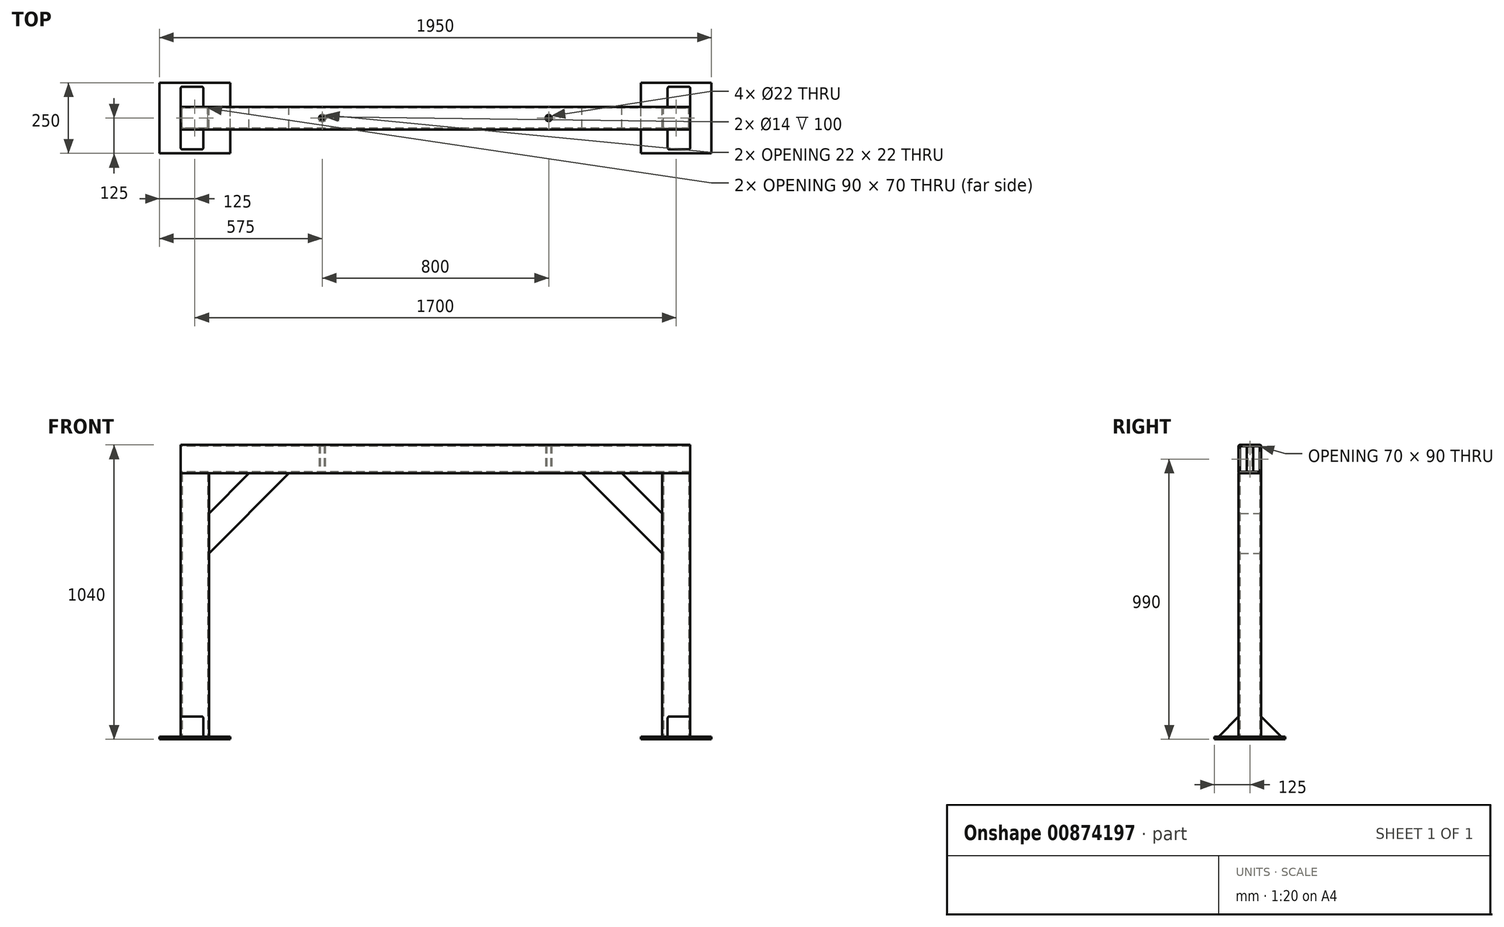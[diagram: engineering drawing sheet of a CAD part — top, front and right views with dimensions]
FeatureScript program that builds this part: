
annotation { "Feature Type Name" : "Feature", "Feature Type Description" : "" }
export const myFeature = defineFeature(function(context is Context, id is Id, definition is map)
    precondition{}
    {
        {
            var Q0;
            Q0=qCreatedBy(makeId("Top.planeOp"),FACE);
            var sketch = newSketch(context, id + "F0", { "sketchPlane" : qUnion([Q0])});
            skLineSegment(sketch, "E0.bottom", {"start": v(-804, -40) * mm, "end": v(-896, -40) * mm});
            skLineSegment(sketch, "E0.top", {"start": v(-804, 40) * mm, "end": v(-896, 40) * mm});
            skLineSegment(sketch, "E0.left", {"start": v(-800, -36) * mm, "end": v(-800, 36) * mm});
            skLineSegment(sketch, "E0.right", {"start": v(-900, -36) * mm, "end": v(-900, 36) * mm});
            skPoint(sketch, "E0.middle", {"position": v(-850, 0) * mm});
            skLineSegment(sketch, "E1.bottom", {"start": v(-808, -35) * mm, "end": v(-892, -35) * mm});
            skLineSegment(sketch, "E1.top", {"start": v(-808, 35) * mm, "end": v(-892, 35) * mm});
            skLineSegment(sketch, "E1.left", {"start": v(-805, -32) * mm, "end": v(-805, 32) * mm});
            skLineSegment(sketch, "E1.right", {"start": v(-895, -32) * mm, "end": v(-895, 32) * mm});
            skPoint(sketch, "E2.visualSharp", {"position": v(-895, 35) * mm});
            skArc(sketch, "E2.filletArc", {"start": v(-892, 35) * mm, "mid": v(-894.12, 34.12) * mm, "end": v(-895, 32) * mm});
            skPoint(sketch, "E3.visualSharp", {"position": v(-805, 35) * mm});
            skArc(sketch, "E3.filletArc", {"start": v(-805, 32) * mm, "mid": v(-805.88, 34.12) * mm, "end": v(-808, 35) * mm});
            skPoint(sketch, "E4.visualSharp", {"position": v(-805, -35) * mm});
            skArc(sketch, "E4.filletArc", {"start": v(-808, -35) * mm, "mid": v(-805.88, -34.12) * mm, "end": v(-805, -32) * mm});
            skPoint(sketch, "E5.visualSharp", {"position": v(-895, -35) * mm});
            skArc(sketch, "E5.filletArc", {"start": v(-895, -32) * mm, "mid": v(-894.12, -34.12) * mm, "end": v(-892, -35) * mm});
            skPoint(sketch, "E6.visualSharp", {"position": v(-900, 40) * mm});
            skArc(sketch, "E6.filletArc", {"start": v(-896, 40) * mm, "mid": v(-898.83, 38.83) * mm, "end": v(-900, 36) * mm});
            skPoint(sketch, "E7.visualSharp", {"position": v(-800, 40) * mm});
            skArc(sketch, "E7.filletArc", {"start": v(-800, 36) * mm, "mid": v(-801.17, 38.83) * mm, "end": v(-804, 40) * mm});
            skPoint(sketch, "E8.visualSharp", {"position": v(-800, -40) * mm});
            skArc(sketch, "E8.filletArc", {"start": v(-804, -40) * mm, "mid": v(-801.17, -38.83) * mm, "end": v(-800, -36) * mm});
            skPoint(sketch, "E9.visualSharp", {"position": v(-900, -40) * mm});
            skArc(sketch, "E9.filletArc", {"start": v(-900, -36) * mm, "mid": v(-898.83, -38.83) * mm, "end": v(-896, -40) * mm});
            skArc(sketch, "E10.MirrorCS", {"start": v(808, -35) * mm, "mid": v(805.88, -34.12) * mm, "end": v(805, -32) * mm});
            skArc(sketch, "E11.MirrorCS", {"start": v(800, 36) * mm, "mid": v(801.17, 38.83) * mm, "end": v(804, 40) * mm});
            skArc(sketch, "E12.MirrorCS", {"start": v(804, -40) * mm, "mid": v(801.17, -38.83) * mm, "end": v(800, -36) * mm});
            skArc(sketch, "E13.MirrorCS", {"start": v(892, 35) * mm, "mid": v(894.12, 34.12) * mm, "end": v(895, 32) * mm});
            skArc(sketch, "E14.MirrorCS", {"start": v(896, 40) * mm, "mid": v(898.83, 38.83) * mm, "end": v(900, 36) * mm});
            skArc(sketch, "E15.MirrorCS", {"start": v(805, 32) * mm, "mid": v(805.88, 34.12) * mm, "end": v(808, 35) * mm});
            skArc(sketch, "E16.MirrorCS", {"start": v(895, -32) * mm, "mid": v(894.12, -34.12) * mm, "end": v(892, -35) * mm});
            skArc(sketch, "E17.MirrorCS", {"start": v(900, -36) * mm, "mid": v(898.83, -38.83) * mm, "end": v(896, -40) * mm});
            skLineSegment(sketch, "E18.MirrorCS", {"start": v(900, -36) * mm, "end": v(900, 36) * mm});
            skPoint(sketch, "E19.MirrorP", {"position": v(850, 0) * mm});
            skLineSegment(sketch, "E20.MirrorCS", {"start": v(804, -40) * mm, "end": v(896, -40) * mm});
            skPoint(sketch, "E21.MirrorP", {"position": v(805, 35) * mm});
            skLineSegment(sketch, "E22.MirrorCS", {"start": v(805, -32) * mm, "end": v(805, 32) * mm});
            skLineSegment(sketch, "E23.MirrorCS", {"start": v(895, -32) * mm, "end": v(895, 32) * mm});
            skLineSegment(sketch, "E24.MirrorCS", {"start": v(800, -36) * mm, "end": v(800, 36) * mm});
            skLineSegment(sketch, "E25.MirrorCS", {"start": v(808, -35) * mm, "end": v(892, -35) * mm});
            skPoint(sketch, "E26.MirrorP", {"position": v(895, 35) * mm});
            skPoint(sketch, "E27.MirrorP", {"position": v(900, 40) * mm});
            skPoint(sketch, "E28.MirrorP", {"position": v(800, 40) * mm});
            skPoint(sketch, "E29.MirrorP", {"position": v(900, -40) * mm});
            skPoint(sketch, "E30.MirrorP", {"position": v(805, -35) * mm});
            skLineSegment(sketch, "E31.MirrorCS", {"start": v(808, 35) * mm, "end": v(892, 35) * mm});
            skLineSegment(sketch, "E32.MirrorCS", {"start": v(804, 40) * mm, "end": v(896, 40) * mm});
            skPoint(sketch, "E33.MirrorP", {"position": v(895, -35) * mm});
            skPoint(sketch, "E34.MirrorP", {"position": v(800, -40) * mm});
            skSolve(sketch);
        }
        {
            var Q0;
            Q0=qSketchRegion(id+"F0",true);
            extrude(context, id + "F1", {"entities" : qUnion([Q0]), "depth" : 930 * mm, "offsetDistance" : 25 * mm});
        }
        {
            var Q0;
            Q0=makeQuery(id+"F1.opExtrude","SWEPT_FACE",FACE,{"disambiguationData":[OSD([sQuery(id+"F0.wireOp",EDGE,"E0.right")])]});
            var sketch = newSketch(context, id + "F2", { "sketchPlane" : qUnion([Q0])});
            skLineSegment(sketch, "E35.bottom", {"start": v(36, 930) * mm, "end": v(-36, 930) * mm});
            skLineSegment(sketch, "E35.top", {"start": v(36, 1030) * mm, "end": v(-36, 1030) * mm});
            skLineSegment(sketch, "E35.left", {"start": v(40, 934) * mm, "end": v(40, 1026) * mm});
            skLineSegment(sketch, "E35.right", {"start": v(-40, 934) * mm, "end": v(-40, 1026) * mm});
            skPoint(sketch, "E35.middle", {"position": v(0, 980) * mm});
            skPoint(sketch, "E35.middle.positionSnap0", {"position": v(0, 930) * mm});
            skPoint(sketch, "E35.centerSnap0", {"position": v(0, 930) * mm});
            skLineSegment(sketch, "E36.bottom", {"start": v(32, 935) * mm, "end": v(-32, 935) * mm});
            skLineSegment(sketch, "E36.top", {"start": v(32, 1025) * mm, "end": v(-32, 1025) * mm});
            skLineSegment(sketch, "E36.left", {"start": v(35, 938) * mm, "end": v(35, 1022) * mm});
            skLineSegment(sketch, "E36.right", {"start": v(-35, 938) * mm, "end": v(-35, 1022) * mm});
            skPoint(sketch, "E37.visualSharp", {"position": v(-35, 1025) * mm});
            skArc(sketch, "E37.filletArc", {"start": v(-32, 1025) * mm, "mid": v(-34.12, 1024.12) * mm, "end": v(-35, 1022) * mm});
            skPoint(sketch, "E38.visualSharp", {"position": v(35, 1025) * mm});
            skArc(sketch, "E38.filletArc", {"start": v(35, 1022) * mm, "mid": v(34.12, 1024.12) * mm, "end": v(32, 1025) * mm});
            skPoint(sketch, "E39.visualSharp", {"position": v(35, 935) * mm});
            skArc(sketch, "E39.filletArc", {"start": v(32, 935) * mm, "mid": v(34.12, 935.88) * mm, "end": v(35, 938) * mm});
            skPoint(sketch, "E40.visualSharp", {"position": v(-35, 935) * mm});
            skArc(sketch, "E40.filletArc", {"start": v(-35, 938) * mm, "mid": v(-34.12, 935.88) * mm, "end": v(-32, 935) * mm});
            skPoint(sketch, "E41.visualSharp", {"position": v(-40, 1030) * mm});
            skArc(sketch, "E41.filletArc", {"start": v(-36, 1030) * mm, "mid": v(-38.83, 1028.83) * mm, "end": v(-40, 1026) * mm});
            skPoint(sketch, "E42.visualSharp", {"position": v(40, 1030) * mm});
            skArc(sketch, "E42.filletArc", {"start": v(40, 1026) * mm, "mid": v(38.83, 1028.83) * mm, "end": v(36, 1030) * mm});
            skPoint(sketch, "E43.visualSharp", {"position": v(40, 930) * mm});
            skArc(sketch, "E43.filletArc", {"start": v(36, 930) * mm, "mid": v(38.83, 931.17) * mm, "end": v(40, 934) * mm});
            skPoint(sketch, "E44.visualSharp", {"position": v(-40, 930) * mm});
            skArc(sketch, "E44.filletArc", {"start": v(-40, 934) * mm, "mid": v(-38.83, 931.17) * mm, "end": v(-36, 930) * mm});
            skSolve(sketch);
        }
        {
            var Q0;
            Q0=makeQuery(id+"F2.imprint","IMPRINT",FACE,{"disambiguationData":[TD([[makeQuery(id+"F2.imprint","IMPRINT",EDGE,{"derivedFrom":sQuery(id+"F2.wireOp",EDGE,"E35.bottom")}),-1.0]])]});
            extrude(context, id + "F3", {"entities" : qUnion([Q0]), "oppositeDirection" : true, "depth" : 1800 * mm, "offsetDistance" : 25 * mm});
        }
        {
            var Q0;
            Q0=qCreatedBy(makeId("Front.planeOp"),FACE);
            var sketch = newSketch(context, id + "F4", { "sketchPlane" : qUnion([Q0])});
            skLineSegment(sketch, "E45.0", {"start": v(800, 788.58) * mm, "end": v(800, 647.16) * mm});
            skLineSegment(sketch, "E46.0", {"start": v(658.58, 930) * mm, "end": v(517.16, 930) * mm});
            skLineSegment(sketch, "E47", {"start": v(800, 647.16) * mm, "end": v(517.16, 930) * mm});
            skLineSegment(sketch, "E48.0", {"start": v(800, 788.58) * mm, "end": v(658.58, 930) * mm});
            skPoint(sketch, "E49.orphan", {"position": v(900, 930) * mm});
            skPoint(sketch, "E50.orphan", {"position": v(-900, 930) * mm});
            skPoint(sketch, "E51.orphan", {"position": v(800, 0) * mm});
            skLineSegment(sketch, "E52.MirrorCS", {"start": v(-800, 788.58) * mm, "end": v(-658.58, 930) * mm});
            skLineSegment(sketch, "E53.MirrorCS", {"start": v(-800, 647.16) * mm, "end": v(-517.16, 930) * mm});
            skLineSegment(sketch, "E54.MirrorCS", {"start": v(-800, 788.58) * mm, "end": v(-800, 647.16) * mm});
            skLineSegment(sketch, "E55.MirrorCS", {"start": v(-658.58, 930) * mm, "end": v(-517.16, 930) * mm});
            skPoint(sketch, "E56.orphan", {"position": v(800, 930) * mm});
            skPoint(sketch, "E57.orphan", {"position": v(-800, 930) * mm});
            skSolve(sketch);
        }
        {
            var Q0;
            Q0=qSketchRegion(id+"F4",true);
            extrude(context, id + "F5", {"entities" : qUnion([Q0]), "endBound" : BoundingType.SYMMETRIC, "depth" : 80 * mm, "offsetDistance" : 25 * mm});
        }
        {
            var Q0;
            Q0=makeQuery(id+"F5.opExtrude","CAP_EDGE",EDGE,{"disambiguationData":[OSD([sQuery(id+"F4.wireOp",EDGE,"E47")])],"isStart":true});
            var Q1;
            Q1=makeQuery(id+"F5.opExtrude","CAP_EDGE",EDGE,{"disambiguationData":[OSD([sQuery(id+"F4.wireOp",EDGE,"E47")])],"isStart":false});
            var Q2;
            Q2=makeQuery(id+"F5.opExtrude","CAP_EDGE",EDGE,{"disambiguationData":[OSD([sQuery(id+"F4.wireOp",EDGE,"E53.MirrorCS")])],"isStart":true});
            var Q3;
            Q3=makeQuery(id+"F5.opExtrude","CAP_EDGE",EDGE,{"disambiguationData":[OSD([sQuery(id+"F4.wireOp",EDGE,"E53.MirrorCS")])],"isStart":false});
            fillet(context, id + "F6", {"entities" : qUnion([Q0, Q1, Q2, Q3]), "radius" : 5 * mm, "tangentPropagation" : true, "allowEdgeOverflow" : false});
        }
        {
            var Q0;
            Q0=makeQuery(id+"F1.opExtrude","CAP_FACE",FACE,{"disambiguationData":[OSD([sQuery(id+"F0.wireOp",EDGE,"E10.MirrorCS"),sQuery(id+"F0.wireOp",EDGE,"E11.MirrorCS"),sQuery(id+"F0.wireOp",EDGE,"E12.MirrorCS"),sQuery(id+"F0.wireOp",EDGE,"E13.MirrorCS"),sQuery(id+"F0.wireOp",EDGE,"E14.MirrorCS"),sQuery(id+"F0.wireOp",EDGE,"E15.MirrorCS"),sQuery(id+"F0.wireOp",EDGE,"E16.MirrorCS"),sQuery(id+"F0.wireOp",EDGE,"E17.MirrorCS"),sQuery(id+"F0.wireOp",EDGE,"E18.MirrorCS"),sQuery(id+"F0.wireOp",EDGE,"E20.MirrorCS"),sQuery(id+"F0.wireOp",EDGE,"E22.MirrorCS"),sQuery(id+"F0.wireOp",EDGE,"E23.MirrorCS"),sQuery(id+"F0.wireOp",EDGE,"E24.MirrorCS"),sQuery(id+"F0.wireOp",EDGE,"E25.MirrorCS"),sQuery(id+"F0.wireOp",EDGE,"E31.MirrorCS"),sQuery(id+"F0.wireOp",EDGE,"E32.MirrorCS")])],"isStart":true});
            var sketch = newSketch(context, id + "F7", { "sketchPlane" : qUnion([Q0])});
            skLineSegment(sketch, "E58.bottom", {"start": v(725, 125) * mm, "end": v(975, 125) * mm});
            skLineSegment(sketch, "E58.top", {"start": v(725, -125) * mm, "end": v(975, -125) * mm});
            skLineSegment(sketch, "E58.left", {"start": v(725, 125) * mm, "end": v(725, -125) * mm});
            skLineSegment(sketch, "E58.right", {"start": v(975, 125) * mm, "end": v(975, -125) * mm});
            skPoint(sketch, "E58.middle", {"position": v(850, 0) * mm});
            skLineSegment(sketch, "E59.MirrorCS", {"start": v(-725, 125) * mm, "end": v(-975, 125) * mm});
            skLineSegment(sketch, "E60.MirrorCS", {"start": v(-725, -125) * mm, "end": v(-975, -125) * mm});
            skLineSegment(sketch, "E61.MirrorCS", {"start": v(-975, 125) * mm, "end": v(-975, -125) * mm});
            skPoint(sketch, "E62.MirrorP", {"position": v(-850, 0) * mm});
            skLineSegment(sketch, "E63.MirrorCS", {"start": v(-725, 125) * mm, "end": v(-725, -125) * mm});
            skSolve(sketch);
        }
        {
            var Q0;
            Q0=qSketchRegion(id+"F7",true);
            extrude(context, id + "F8", {"entities" : qUnion([Q0]), "depth" : 10 * mm, "offsetDistance" : 25 * mm});
        }
        {
            var Q0;
            Q0=makeQuery(id+"F1.opExtrude","SWEPT_FACE",FACE,{"disambiguationData":[OSD([sQuery(id+"F0.wireOp",EDGE,"E18.MirrorCS")])]});
            var sketch = newSketch(context, id + "F9", { "sketchPlane" : qUnion([Q0])});
            skLineSegment(sketch, "E64.0", {"start": v(40, 70.71) * mm, "end": v(40, 0) * mm});
            skLineSegment(sketch, "E65.0", {"start": v(40, 0) * mm, "end": v(110.71, 0) * mm});
            skLineSegment(sketch, "E66", {"start": v(40, 70.71) * mm, "end": v(110.71, 0) * mm});
            skPoint(sketch, "E67.orphan", {"position": v(40, 930) * mm});
            skPoint(sketch, "E68.orphan", {"position": v(125, 0) * mm});
            skPoint(sketch, "E69.orphan", {"position": v(-125, 0) * mm});
            skLineSegment(sketch, "E70.MirrorCS", {"start": v(-40, 70.71) * mm, "end": v(-110.71, 0) * mm});
            skLineSegment(sketch, "E71.MirrorCS", {"start": v(-40, 0) * mm, "end": v(-110.71, 0) * mm});
            skLineSegment(sketch, "E72.MirrorCS", {"start": v(-40, 70.71) * mm, "end": v(-40, 0) * mm});
            skSolve(sketch);
        }
        {
            var Q0;
            Q0=makeQuery(id+"F9.imprint","IMPRINT",FACE,{"disambiguationData":[TD([[makeQuery(id+"F9.imprint","IMPRINT",EDGE,{"derivedFrom":sQuery(id+"F9.wireOp",EDGE,"E70.MirrorCS")}),1.0]])]});
            var Q1;
            Q1=makeQuery(id+"F9.imprint","IMPRINT",FACE,{"disambiguationData":[TD([[makeQuery(id+"F9.imprint","IMPRINT",EDGE,{"derivedFrom":sQuery(id+"F9.wireOp",EDGE,"E64.0")}),1.0]])]});
            extrude(context, id + "F10", {"entities" : qUnion([Q0, Q1]), "oppositeDirection" : true, "depth" : 80 * mm, "offsetDistance" : 25 * mm});
        }
        {
            var Q0;
            Q0=makeQuery(id+"F10.opExtrude","CAP_EDGE",EDGE,{"disambiguationData":[OSD([sQuery(id+"F9.wireOp",EDGE,"E66")])],"isStart":true});
            var Q1;
            Q1=makeQuery(id+"F10.opExtrude","CAP_EDGE",EDGE,{"disambiguationData":[OSD([sQuery(id+"F9.wireOp",EDGE,"E66")])],"isStart":false});
            var Q2;
            Q2=makeQuery(id+"F10.opExtrude","CAP_EDGE",EDGE,{"disambiguationData":[OSD([sQuery(id+"F9.wireOp",EDGE,"E70.MirrorCS")])],"isStart":true});
            var Q3;
            Q3=makeQuery(id+"F10.opExtrude","CAP_EDGE",EDGE,{"disambiguationData":[OSD([sQuery(id+"F9.wireOp",EDGE,"E70.MirrorCS")])],"isStart":false});
            fillet(context, id + "F11", {"entities" : qUnion([Q0, Q1, Q2, Q3]), "radius" : 5 * mm, "tangentPropagation" : true, "allowEdgeOverflow" : false});
        }
        {
            var Q0;
            Q0=makeQuery(id+"F10.opExtrude","SWEPT_BODY",BODY,{"disambiguationData":[OSD([sQuery(id+"F9.wireOp",EDGE,"E70.MirrorCS"),sQuery(id+"F9.wireOp",EDGE,"E71.MirrorCS"),sQuery(id+"F9.wireOp",EDGE,"E72.MirrorCS")])]});
            var Q1;
            Q1=makeQuery(id+"F10.opExtrude","SWEPT_BODY",BODY,{"disambiguationData":[OSD([sQuery(id+"F9.wireOp",EDGE,"E64.0"),sQuery(id+"F9.wireOp",EDGE,"E65.0"),sQuery(id+"F9.wireOp",EDGE,"E66")])]});
            var Q2;
            Q2=qCreatedBy(makeId("Right.planeOp"),FACE);
            mirror(context, id + "F12", {"entities" : qUnion([Q0, Q1]), "mirrorPlane" : qUnion([Q2])});
        }
        {
            var Q0;
            Q0=makeQuery(id+"F3.opExtrude","SWEPT_FACE",FACE,{"disambiguationData":[OSD([sQuery(id+"F2.wireOp",EDGE,"E35.bottom")])]});
            var sketch = newSketch(context, id + "F13", { "sketchPlane" : qUnion([Q0])});
            skCircle(sketch, "E73", {"center": v(-400, 0) * mm, "radius": 11 * mm});
            skCircle(sketch, "E74.MirrorC", {"center": v(400, 0) * mm, "radius": 11 * mm});
            skSolve(sketch);
        }
        {
            var Q0;
            Q0=qSketchRegion(id+"F13",true);
            extrude(context, id + "F14", {"entities" : qUnion([Q0]), "operationType" : NewBodyOperationType.REMOVE, "oppositeDirection" : true, "depth" : 100 * mm, "offsetDistance" : 25 * mm});
        }
        {
            var Q0;
            Q0=makeQuery(id+"F3.opExtrude","SWEPT_FACE",FACE,{"disambiguationData":[OSD([sQuery(id+"F2.wireOp",EDGE,"E35.bottom")])]});
            var sketch = newSketch(context, id + "F15", { "sketchPlane" : qUnion([Q0])});
            skCircle(sketch, "E75", {"center": v(-400, 0) * mm, "radius": 11 * mm});
            skCircle(sketch, "E76", {"center": v(-400, 0) * mm, "radius": 7 * mm});
            skCircle(sketch, "E77.MirrorC", {"center": v(400, 0) * mm, "radius": 11 * mm});
            skCircle(sketch, "E78.MirrorC", {"center": v(400, 0) * mm, "radius": 7 * mm});
            skSolve(sketch);
        }
        {
            var Q0;
            Q0=qSketchRegion(id+"F15",true);
            extrude(context, id + "F16", {"entities" : qUnion([Q0]), "oppositeDirection" : true, "depth" : 100 * mm, "offsetDistance" : 25 * mm});
        }
        {
            var Q0;
            Q0=makeQuery(id+"F5.opExtrude","CAP_EDGE",EDGE,{"disambiguationData":[OSD([sQuery(id+"F4.wireOp",EDGE,"E52.MirrorCS")])],"isStart":false});
            var Q1;
            Q1=makeQuery(id+"F5.opExtrude","CAP_EDGE",EDGE,{"disambiguationData":[OSD([sQuery(id+"F4.wireOp",EDGE,"E52.MirrorCS")])],"isStart":true});
            fillet(context, id + "F17", {"entities" : qUnion([Q0, Q1]), "radius" : 5 * mm, "tangentPropagation" : true, "allowEdgeOverflow" : false});
        }
        {
            var Q0;
            Q0=makeQuery(id+"F5.opExtrude","CAP_EDGE",EDGE,{"disambiguationData":[OSD([sQuery(id+"F4.wireOp",EDGE,"E48.0")])],"isStart":true});
            var Q1;
            Q1=makeQuery(id+"F5.opExtrude","CAP_EDGE",EDGE,{"disambiguationData":[OSD([sQuery(id+"F4.wireOp",EDGE,"E48.0")])],"isStart":false});
            fillet(context, id + "F18", {"entities" : qUnion([Q0, Q1]), "radius" : 5 * mm, "tangentPropagation" : true, "allowEdgeOverflow" : false});
        }
    });
